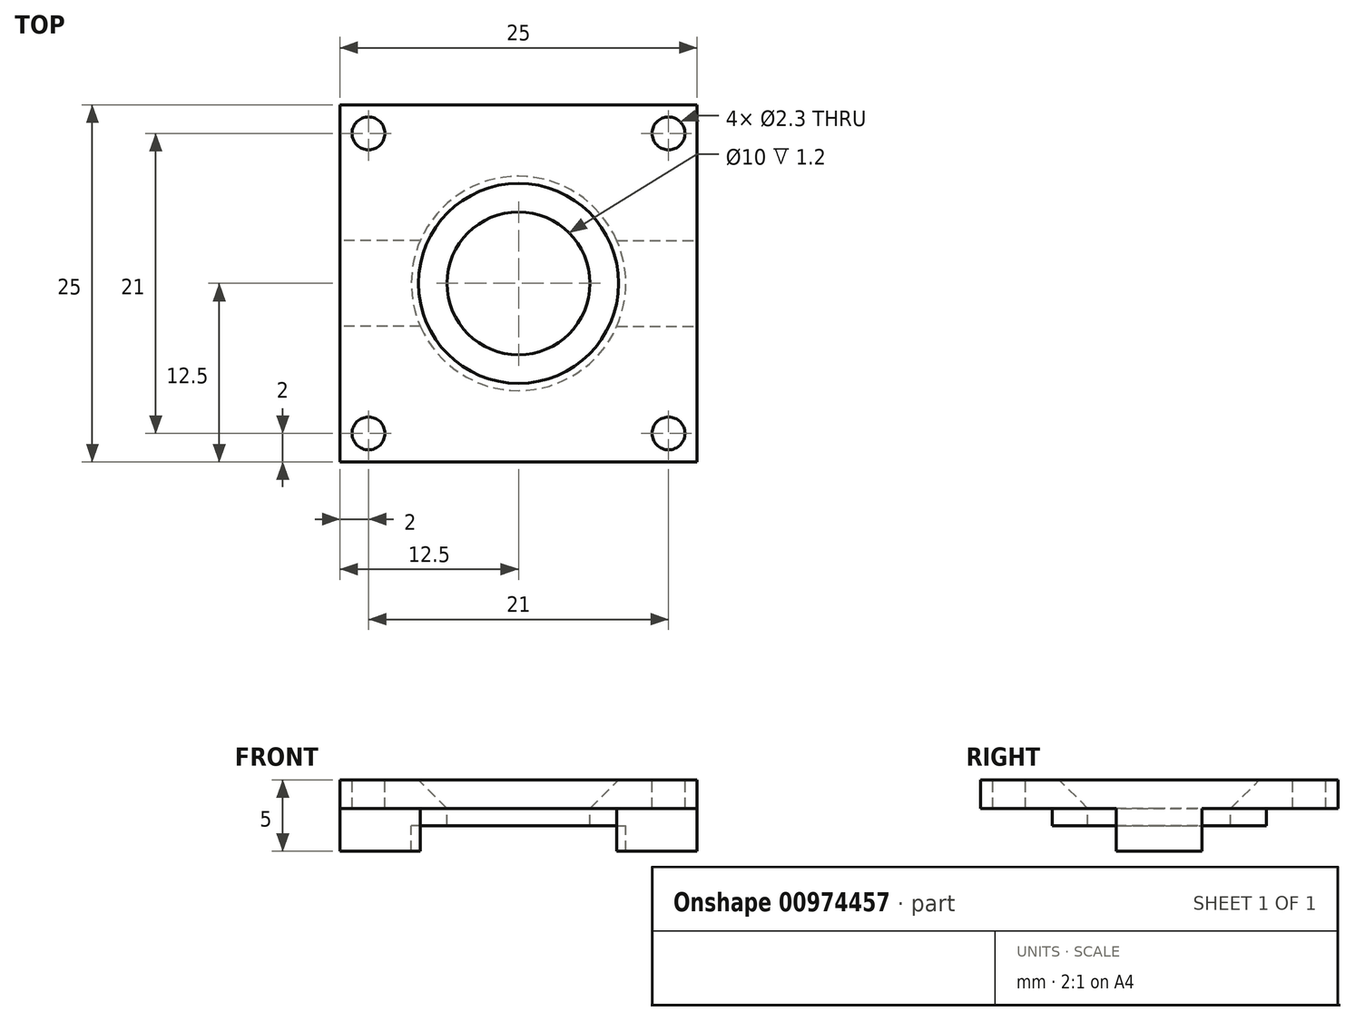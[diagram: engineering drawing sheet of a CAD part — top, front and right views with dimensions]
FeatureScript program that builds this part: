
annotation { "Feature Type Name" : "Feature", "Feature Type Description" : "" }
export const myFeature = defineFeature(function(context is Context, id is Id, definition is map)
    precondition{}
    {
        {
            var Q0;
            Q0=qCreatedBy(makeId("Top.planeOp"),FACE);
            var sketch = newSketch(context, id + "F0", { "sketchPlane" : qUnion([Q0])});
            skCircle(sketch, "E0", {"center": v(0, 0) * mm, "radius": 5 * mm});
            skCircle(sketch, "E1", {"center": v(0, 0) * mm, "radius": 7.5 * mm});
            skLineSegment(sketch, "E2.bottom", {"start": v(-12.5, 12.5) * mm, "end": v(12.5, 12.5) * mm});
            skLineSegment(sketch, "E2.top", {"start": v(-12.5, -12.5) * mm, "end": v(12.5, -12.5) * mm});
            skLineSegment(sketch, "E2.left", {"start": v(-12.5, 12.5) * mm, "end": v(-12.5, -12.5) * mm});
            skLineSegment(sketch, "E2.right", {"start": v(12.5, 12.5) * mm, "end": v(12.5, -12.5) * mm});
            skLineSegment(sketch, "E3", {"start": v(-6.87, 3) * mm, "end": v(-12.5, 3) * mm});
            skLineSegment(sketch, "E4", {"start": v(-12.5, 12.5) * mm, "end": v(12.5, -12.5) * mm, "construction": true});
            skLineSegment(sketch, "E5", {"start": v(12.5, 12.5) * mm, "end": v(-12.5, -12.5) * mm, "construction": true});
            skCircle(sketch, "E6", {"center": v(-10.5, 10.5) * mm, "radius": 1.15 * mm});
            skCircle(sketch, "E7.MirrorC", {"center": v(-10.5, -10.5) * mm, "radius": 1.15 * mm});
            skLineSegment(sketch, "E8.MirrorCS", {"start": v(-6.87, -3) * mm, "end": v(-12.5, -3) * mm});
            skCircle(sketch, "E9.MirrorC", {"center": v(10.5, 10.5) * mm, "radius": 1.15 * mm});
            skLineSegment(sketch, "E10.MirrorCS", {"start": v(6.87, 3) * mm, "end": v(12.5, 3) * mm});
            skLineSegment(sketch, "E11.MirrorCS", {"start": v(6.87, -3) * mm, "end": v(12.5, -3) * mm});
            skCircle(sketch, "E12.MirrorC", {"center": v(10.5, -10.5) * mm, "radius": 1.15 * mm});
            skSolve(sketch);
        }
        {
            var Q0;
            Q0=makeQuery(id+"F0.imprint","IMPRINT",FACE,{"disambiguationData":[TD([[makeQuery(id+"F0.imprint","IMPRINT",EDGE,{"derivedFrom":sQuery(id+"F0.wireOp",EDGE,"E0")}),-1.0]])]});
            extrude(context, id + "F1", {"entities" : qUnion([Q0]), "depth" : 3.2 * mm, "offsetDistance" : 25 * mm});
        }
        {
            var Q0;
            {var subQ1=sQuery(id+"F0.wireOp",EDGE,"E2.bottom");Q0=makeQuery(id+"F0.imprint","IMPRINT",FACE,{"disambiguationData":[TD([[makeQuery(id+"F0.imprint","IMPRINT",EDGE,{"derivedFrom":subQ1}),-1.0]])]});}
            var Q1;
            {var subQ1=sQuery(id+"F0.wireOp",EDGE,"E2.top");Q1=makeQuery(id+"F0.imprint","IMPRINT",FACE,{"disambiguationData":[TD([[makeQuery(id+"F0.imprint","IMPRINT",EDGE,{"derivedFrom":subQ1}),1.0]])]});}
            extrude(context, id + "F2", {"entities" : qUnion([Q0, Q1]), "operationType" : NewBodyOperationType.ADD, "depth" : 2 * mm, "offsetDistance" : 25 * mm});
        }
        {
            var Q0;
            {var subQ0=sQuery(id+"F0.wireOp",EDGE,"E3");Q0=makeQuery(id+"F0.imprint","IMPRINT",FACE,{"disambiguationData":[TD([[makeQuery(id+"F0.imprint","IMPRINT",EDGE,{"derivedFrom":subQ0}),1.0]])]});}
            var Q1;
            {var subQ0=sQuery(id+"F0.wireOp",EDGE,"E10.MirrorCS");Q1=makeQuery(id+"F0.imprint","IMPRINT",FACE,{"disambiguationData":[TD([[makeQuery(id+"F0.imprint","IMPRINT",EDGE,{"derivedFrom":subQ0}),-1.0]])]});}
            extrude(context, id + "F3", {"entities" : qUnion([Q0, Q1]), "operationType" : NewBodyOperationType.ADD, "depth" : 5 * mm, "offsetDistance" : 25 * mm});
        }
        {
            var Q0;
            Q0=makeQuery(id+"F1.opExtrude","CAP_EDGE",EDGE,{"disambiguationData":[OSD([sQuery(id+"F0.wireOp",EDGE,"E0")])],"isStart":true});
            chamfer(context, id + "F4", {"entities" : qUnion([Q0]), "width" : 2 * mm, "tangentPropagation" : true});
        }
        {
            var Q0;
            Q0=makeQuery(id+"F1.opExtrude","SWEPT_BODY",BODY,{"disambiguationData":[OSD([sQuery(id+"F0.wireOp",EDGE,"E0"),sQuery(id+"F0.wireOp",EDGE,"E1")])]});
            var Q1;
            Q1=makeQuery(id+"F3.opExtrude","CAP_EDGE",EDGE,{"disambiguationData":[OSD([sQuery(id+"F0.wireOp",EDGE,"E11.MirrorCS")])],"isStart":false});
            transform(context, id + "F5", {"entities" : qUnion([Q0]), "transformType" : TransformType.ROTATION, "transformAxis" : qUnion([Q1]), "angle" : 180 * degree, "makeCopy" : false});
        }
    });
